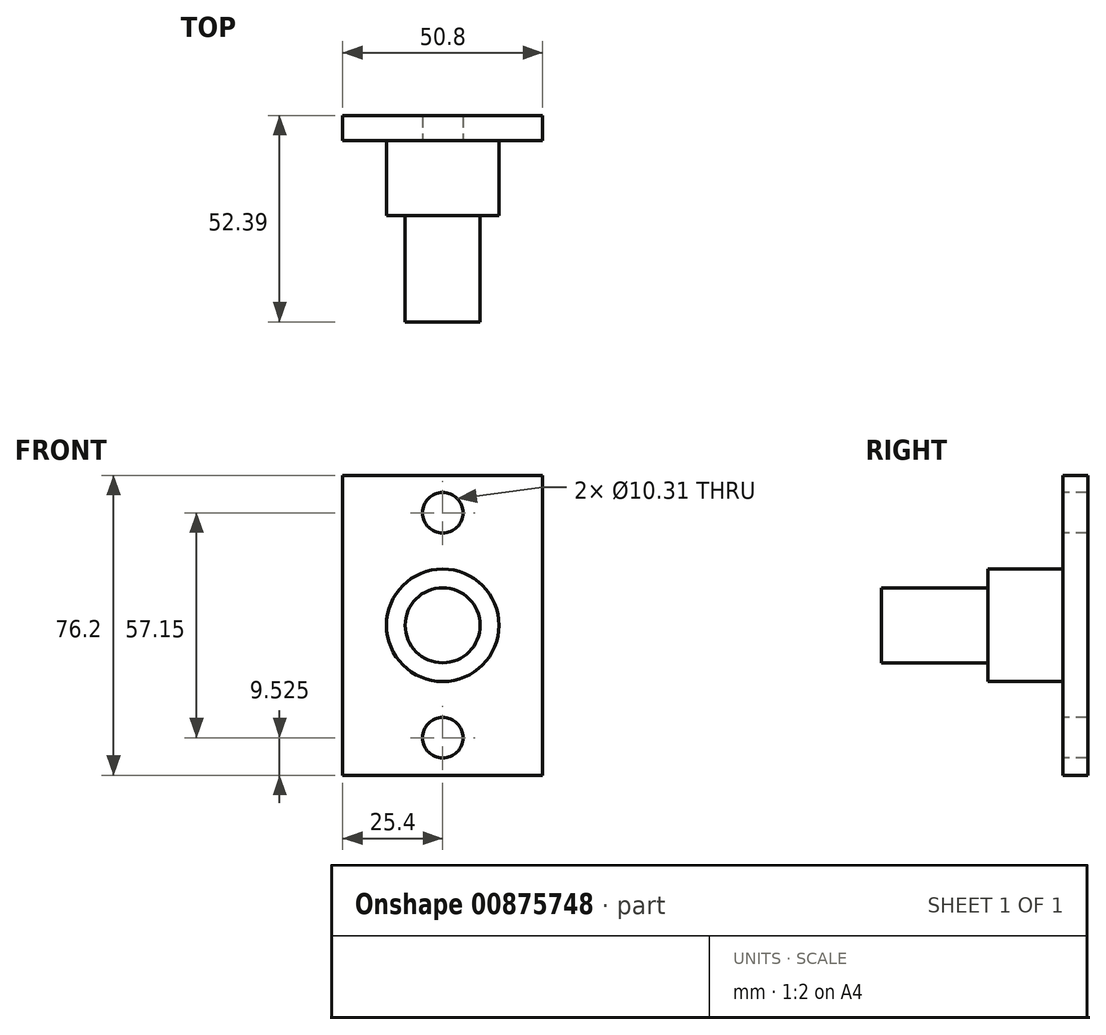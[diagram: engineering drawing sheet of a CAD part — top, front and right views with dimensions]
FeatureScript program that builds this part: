
annotation { "Feature Type Name" : "Feature", "Feature Type Description" : "" }
export const myFeature = defineFeature(function(context is Context, id is Id, definition is map)
    precondition{}
    {
        {
            var Q0;
            Q0=qCreatedBy(makeId("Front.planeOp"),FACE);
            var sketch = newSketch(context, id + "F0", { "sketchPlane" : qUnion([Q0])});
            skLineSegment(sketch, "E0.bottom", {"start": v(25.4, 38.1) * mm, "end": v(-25.4, 38.1) * mm});
            skLineSegment(sketch, "E0.top", {"start": v(25.4, -38.1) * mm, "end": v(-25.4, -38.1) * mm});
            skLineSegment(sketch, "E0.left", {"start": v(25.4, 38.1) * mm, "end": v(25.4, -38.1) * mm});
            skLineSegment(sketch, "E0.right", {"start": v(-25.4, 38.1) * mm, "end": v(-25.4, -38.1) * mm});
            skPoint(sketch, "E0.middle", {"position": v(0, 0) * mm});
            skPoint(sketch, "E1", {"position": v(0, 28.58) * mm});
            skPoint(sketch, "E2", {"position": v(0, -28.58) * mm});
            skSolve(sketch);
        }
        {
            var Q0;
            Q0 = qSketchRegion(id + "F0", true);
            extrude(context, id + "F1", {"entities" : qUnion([Q0]), "depth" : 6.35 * mm, "offsetDistance" : 25.4 * mm});
        }
        {
            var Q0;
            Q0=sQuery(id+"F0.wireOp",VERTEX,"E1");
            var Q1;
            Q1=sQuery(id+"F0.wireOp",VERTEX,"E2");
            var Q2;
            Q2=makeQuery(id+"F1.opExtrude","SWEPT_BODY",BODY,{"disambiguationData":[OSD([sQuery(id+"F0.wireOp",EDGE,"E0.bottom"),sQuery(id+"F0.wireOp",EDGE,"E0.top"),sQuery(id+"F0.wireOp",EDGE,"E0.left"),sQuery(id+"F0.wireOp",EDGE,"E0.right")])]});
            hole(context, id + "F2", {"style" : HoleStyle.SIMPLE, "endStyle" : HoleEndStyle.THROUGH, "oppositeDirection" : true, "standardTappedOrClearance" : lookupTablePath({ "fit" : "Normal (ASME)", "standard" : "ANSI", "size" : "3/8", "type" : "Clearance" }), "standardBlindInLast" : lookupTablePath({ "fit" : "Normal", "standard" : "ANSI", "engagement" : "75%", "pitch" : "16 tpi", "size" : "3/8", "type" : "Clearance & tapped" }), "holeDiameter" : 10.3 * mm, "majorDiameter" : 6.35 * mm, "isTappedThrough" : true, "tappedDepth" : 12.7 * mm, "tapClearance" : 3, "locations" : qUnion([Q0, Q1]), "scope" : qUnion([Q2])});
        }
        {
            var Q0;
            Q0=makeQuery(id+"F1.opExtrude","CAP_FACE",FACE,{"disambiguationData":[OSD([sQuery(id+"F0.wireOp",EDGE,"E0.bottom"),sQuery(id+"F0.wireOp",EDGE,"E0.top"),sQuery(id+"F0.wireOp",EDGE,"E0.left"),sQuery(id+"F0.wireOp",EDGE,"E0.right")])],"isStart":false});
            var sketch = newSketch(context, id + "F3", { "sketchPlane" : qUnion([Q0])});
            skCircle(sketch, "E3", {"center": v(0, 0) * mm, "radius": 14.29 * mm});
            skSolve(sketch);
        }
        {
            var Q0;
            Q0=makeQuery(id+"F3.imprint","IMPRINT",FACE,{"disambiguationData":[TD([[makeQuery(id+"F3.imprint","IMPRINT",EDGE,{"derivedFrom":sQuery(id+"F3.wireOp",EDGE,"E3")}),1.0]])]});
            extrude(context, id + "F4", {"entities" : qUnion([Q0]), "operationType" : NewBodyOperationType.ADD, "depth" : 19.05 * mm, "offsetDistance" : 25.4 * mm});
        }
        {
            var Q0;
            Q0=makeQuery(id+"F4.opExtrude","CAP_FACE",FACE,{"disambiguationData":[OSD([sQuery(id+"F3.wireOp",EDGE,"E3")])],"isStart":false});
            var sketch = newSketch(context, id + "F5", { "sketchPlane" : qUnion([Q0])});
            skCircle(sketch, "E4", {"center": v(0, 0) * mm, "radius": 9.53 * mm});
            skSolve(sketch);
        }
        {
            var Q0;
            Q0 = qSketchRegion(id + "F5", true);
            extrude(context, id + "F6", {"entities" : qUnion([Q0]), "operationType" : NewBodyOperationType.ADD, "depth" : 26.99 * mm, "offsetDistance" : 25.4 * mm});
        }
    });
